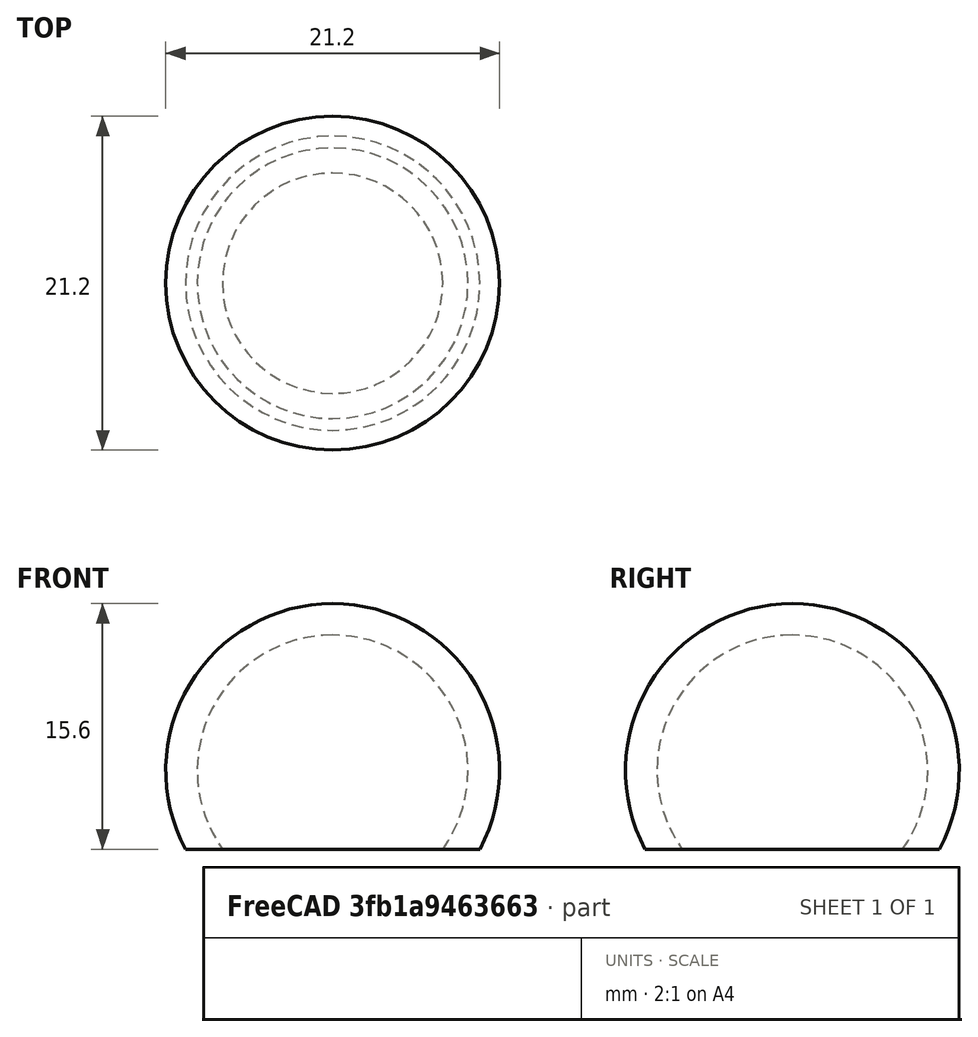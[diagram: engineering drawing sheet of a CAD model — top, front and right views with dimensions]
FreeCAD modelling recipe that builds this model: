
FCSTD DOCUMENT  (FreeCAD 0.20R29177 (Git))
Label: bun bolt connector
License: All rights reserved
LicenseURL: http://en.wikipedia.org/wiki/All_rights_reserved
objects: Part::Sphere×2, Part::Cut×2, PartDesign::Body×1, Part::Box×1
note: 6 computed .brp shape members not serialized (recipe doc carries the construction recipe); baked Part::Feature solids carry a one-line shape summary decoded from their .brp

FEATURE [PartDesign::Body] Body
  Origin = -> Origin
FEATURE [Part::Sphere] Sphere  label="Topuz"
  Angle1 = -90
  Angle2 = 90
  Angle3 = 360
  AttacherType = Attacher::AttachEngine3D
  Placement = pos=(0,0,15) rot=(0,0,1;0rad)
  Radius = 8.6
FEATURE [Part::Sphere] Sphere001  label="Sphere"
  Angle1 = -90
  Angle2 = 90
  Angle3 = 360
  AttacherType = Attacher::AttachEngine3D
  Placement = pos=(0,0,15) rot=(0,0,1;0rad)
  Radius = 10.6
FEATURE [Part::Cut] Cut
  Base = -> Sphere001
  Tool = -> Sphere
FEATURE [Part::Box] Box  label="Cube"
  AttacherType = Attacher::AttachEngine3D
  Height = 9
  Length = 20
  Placement = pos=(-10,-10,1) rot=(0,0,1;0rad)
  Width = 20
FEATURE [Part::Cut] Cut001  label="Rouded"
  Base = -> Cut
  Tool = -> Box
